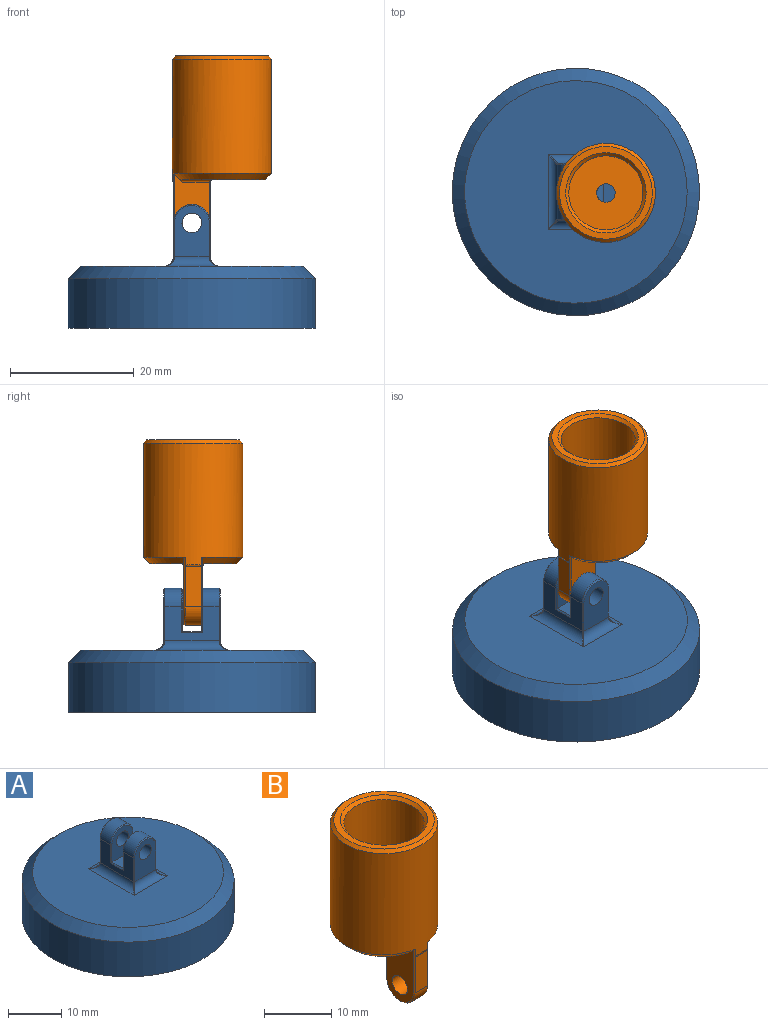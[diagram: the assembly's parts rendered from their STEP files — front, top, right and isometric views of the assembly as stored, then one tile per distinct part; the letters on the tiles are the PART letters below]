
ASSEMBLY  parts=2 mates=1
PART A: 39 faces, bbox 40x40x20 mm
  f0: plane 8.8x5.5mm, normal (-1,0,0), area 34.1mm2, adj f12,f13,f16,f22,f29,f31,f33,f35
  f1: plane 36x36mm, normal (0,0,1), area 908.1mm2, adj f16,f17,f18,f19,f20
  f2: cylinder r=20mm len=40mm, axis (0,0,-1), area 1005.3mm2, adj f3,f20
  f3: plane 40x40mm, normal (0,0,-1), area 549.8mm2, adj f2,f4
  f4: cylinder r=15mm len=30mm, axis (0,0,-1), area 754mm2, adj f3,f5
  f5: plane 30x30mm, normal (0,0,-1), area 706.9mm2, adj f4
  f6: plane 8.3x5.6mm, normal (0,-1,0), area 35.1mm2, adj f15,f17,f22,f23,f24
  f7: plane 8.8x5.5mm, normal (1,0,0), area 34.1mm2, adj f12,f13,f19,f24,f27,f34,f36,f38
  f8: plane 8.3x5.6mm, normal (0,1,0), area 35.1mm2, adj f14,f18,f27,f28,f29
  f9: plane 6.8x5.6mm, normal (0,1,0), area 26.7mm2, adj f11,f15,f31,f32,f34
  f10: plane 6.8x5.6mm, normal (0,-1,0), area 26.7mm2, adj f11,f14,f35,f37,f38
  f11: plane 5.6x3mm, normal (0,0,1), area 16.8mm2, adj f9,f10,f33,f36
  f12: cylinder r=3mm len=6mm, axis (0,-1,0), area 25.4mm2, adj f0,f7,f28,f37
  f13: cylinder r=3mm len=6mm, axis (0,1,0), area 25.4mm2, adj f0,f7,f23,f32
  f14: cylinder r=1.6mm len=3.2mm, axis (0,1,0), area 31.2mm2, adj f8,f10
  f15: cylinder r=1.6mm len=3.2mm, axis (0,1,0), area 31.2mm2, adj f6,f9
  f16: cylinder r=1.5mm len=12.2mm, axis (0,-1,0), area 24.7mm2, adj f0,f1,f21,f30
  f17: cylinder r=1.5mm len=9mm, axis (1,0,0), area 17.2mm2, adj f1,f6,f21,f25
  f18: cylinder r=1.5mm len=9mm, axis (-1,0,0), area 17.2mm2, adj f1,f8,f26,f30
  f19: cylinder r=1.5mm len=12.2mm, axis (0,1,0), area 24.7mm2, adj f1,f7,f25,f26
  f20: cone r=18mm half-angle=45deg, axis (0,0,-1), area 337.7mm2, adj f1,f2
  f21: bspline ~1.7x1.7mm, area 0.3mm2, adj f16,f17,f22
  f22: plane 5.5x0.2mm, normal (-0.71,-0.71,0), area 1.6mm2, adj f0,f6,f21,f23
  f23: cone r=2.8mm half-angle=45deg, axis (0,1,0), area 2.6mm2, adj f6,f13,f22,f24
  f24: plane 5.5x0.2mm, normal (0.71,-0.71,0), area 1.6mm2, adj f6,f7,f23,f25
  f25: bspline ~1.7x1.7mm, area 0.3mm2, adj f17,f19,f24
  f26: bspline ~1.7x1.7mm, area 0.3mm2, adj f18,f19,f27
  f27: plane 5.5x0.2mm, normal (0.71,0.71,0), area 1.6mm2, adj f7,f8,f26,f28
  f28: cone r=2.8mm half-angle=45deg, axis (0,-1,0), area 2.6mm2, adj f8,f12,f27,f29
  f29: plane 5.5x0.2mm, normal (-0.71,0.71,0), area 1.6mm2, adj f0,f8,f28,f30
  f30: bspline ~1.7x1.7mm, area 0.3mm2, adj f16,f18,f29
  f31: plane 4.2x0.2mm, normal (-0.71,0.71,0), area 1.2mm2, adj f0,f9,f32,f33
  f32: cone r=2.8mm half-angle=45deg, axis (0,-1,0), area 2.6mm2, adj f9,f13,f31,f34
  f33: plane 3.4x0.2mm, normal (-0.71,0,0.71), area 0.9mm2, adj f0,f11,f31,f35
  f34: plane 4.2x0.2mm, normal (0.71,0.71,0), area 1.2mm2, adj f7,f9,f32,f36
  f35: plane 4.2x0.2mm, normal (-0.71,-0.71,0), area 1.2mm2, adj f0,f10,f33,f37
  f36: plane 3.4x0.2mm, normal (0.71,0,0.71), area 0.9mm2, adj f7,f11,f34,f38
  f37: cone r=2.8mm half-angle=45deg, axis (0,1,0), area 2.6mm2, adj f10,f12,f35,f38
  f38: plane 4.2x0.2mm, normal (0.71,-0.71,0), area 1.2mm2, adj f7,f10,f36,f37
PART B: 30 faces, bbox 20000000000000000038313501714693374724319102545303840223056070291987586484079775119224722902163606470656x20000000000000000038313501714693374724319102545303840223056070291987586484079775119224722902163606470656x20000000000000000038313501714693374724319102545303840223056070291987586484079775119224722902163606470656 mm
  f0: cylinder r=0.5mm len=2.6mm, axis (1,0,0), area 0.8mm2, adj f1,f26,f27,f28
  f1: plane 6.5x2.6mm, normal (0,-1,0), area 16.9mm2, adj f0,f2,f26,f28
  f2: cylinder r=3mm len=6mm, axis (-1,0,0), area 24.5mm2, adj f1,f3,f24,f25
  f3: cone r=2.8mm half-angle=45deg, axis (-1,0,0), area 2.6mm2, adj f2,f4,f23,f26
  f4: plane 10.63x5.63mm, normal (1,0,0), area 41.5mm2, adj f3,f5,f21,f22,f23,f26
  f5: cylinder r=0.5mm len=5.35mm, axis (0,1,0), area 3.8mm2, adj f4,f6,f20,f21
  f6: bspline ~0.71x0.71mm, area 0.1mm2, adj f5,f7,f23
  f7: cylinder r=0.5mm len=1.36mm, axis (-1,0,0), area 0.8mm2, adj f6,f8,f20,f24
  f8: bspline ~1.79x0.66mm, area 0.9mm2, adj f7,f9,f14,f24
  f9: cylinder r=0.5mm len=1.36mm, axis (-1,0,0), area 0.8mm2, adj f8,f10,f20,f24
  f10: bspline ~0.71x0.71mm, area 0.1mm2, adj f9,f11,f13
  f11: cylinder r=0.5mm len=5.35mm, axis (0,-1,0), area 3.8mm2, adj f10,f12,f20,f21
  f12: plane 10.63x5.63mm, normal (-1,0,0), area 41.5mm2, adj f11,f13,f21,f22,f25,f28
  f13: plane 6.5x0.2mm, normal (-0.71,0.71,0), area 1.8mm2, adj f10,f12,f24,f25
  f14: cylinder r=1.5mm len=3mm, axis (0,0,1), area 18.8mm2, adj f8,f15,f20
  f15: plane 12x12mm, normal (0,0,1), area 106mm2, adj f14,f16
  f16: cylinder r=6mm len=17.5mm, axis (0,0,1), area 659.7mm2, adj f15,f17
  f17: cone r=6mm half-angle=45deg, axis (0,0,1), area 27.8mm2, adj f16,f18
  f18: plane 15x15mm, normal (0,0,1), area 44mm2, adj f17,f19
  f19: cone r=7.5mm half-angle=45deg, axis (0,0,-1), area 34.4mm2, adj f18,f27
  f20: plane 14x13.71mm, normal (0,0,-1), area 124.8mm2, adj f5,f7,f9,f11,f14,f21
  f21: cone r=8mm half-angle=45deg, axis (0,0,1), area 62.6mm2, adj f4,f5,f11,f12,f20,f26,f27,f28
  f22: cylinder r=1.6mm len=3.2mm, axis (1,0,0), area 30.2mm2, adj f4,f12
  f23: plane 6.5x0.2mm, normal (0.71,0.71,0), area 1.8mm2, adj f3,f4,f6,f24
  f24: plane 6.52x2.6mm, normal (0,1,0), area 16.9mm2, adj f2,f7,f8,f9,f13,f23
  f25: cone r=2.8mm half-angle=45deg, axis (1,0,0), area 2.6mm2, adj f2,f12,f13,f28
  f26: plane 8.02x0.26mm, normal (0.71,-0.71,0), area 2.3mm2, adj f0,f1,f3,f4,f21,f27
  f27: cylinder r=8mm len=19.8mm, axis (0,0,-1), area 933.2mm2, adj f0,f19,f21,f26,f28
  f28: plane 8.02x0.26mm, normal (-0.71,-0.71,0), area 2.3mm2, adj f0,f1,f12,f21,f25,f27
  f29: cylinder r=8mm len=20000000000000000038313501714693374724319102545303840223056070291987586484079775119224722902163606470656mm, axis (0,0,-1), area 640000000000000001226032054870187991178211281449722887137794249343602767490552803815191132869235407060992mm2
PLACE A t=(-13.9,-2.61,-1.72)mm
PLACE B rot(axis=(0,0,-1),90deg) t=(-9.05,-2.81,22.28)mm
MATE revolute B.f3 <-> A.f12  axis (0,-1,0) through (-13.9,-4.31,15.28)mm
